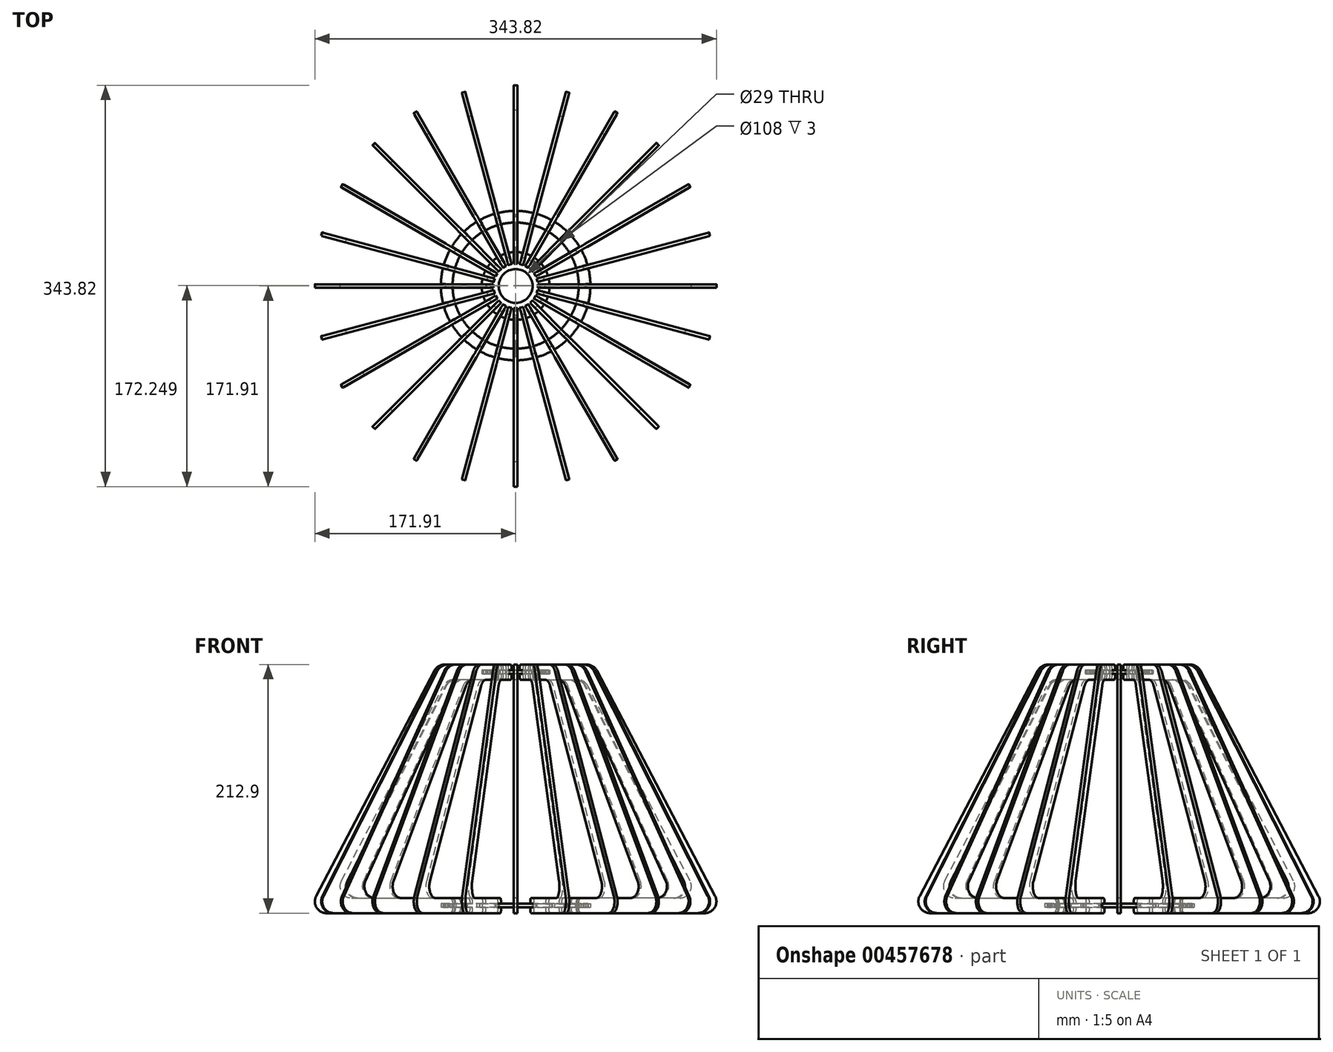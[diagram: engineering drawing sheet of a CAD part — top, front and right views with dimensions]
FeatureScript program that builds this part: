
annotation { "Feature Type Name" : "Feature", "Feature Type Description" : "" }
export const myFeature = defineFeature(function(context is Context, id is Id, definition is map)
    precondition{}
    {
        {
            var Q0;
            Q0=qCreatedBy(makeId("Top.planeOp"),FACE);
            var sketch = newSketch(context, id + "F0", { "sketchPlane" : qUnion([Q0])});
            skCircle(sketch, "E0", {"center": v(0, 0) * mm, "radius": 14.5 * mm});
            skArc(sketch, "E1", {"start": v(-1.45, 29) * mm, "mid": v(-3.79, 28.79) * mm, "end": v(-6.1, 28.39) * mm});
            skLineSegment(sketch, "E2", {"start": v(-1.45, 29) * mm, "end": v(-1.45, 25) * mm});
            skLineSegment(sketch, "E3", {"start": v(-1.45, 25) * mm, "end": v(1.45, 25) * mm});
            skLineSegment(sketch, "E4", {"start": v(1.45, 25) * mm, "end": v(1.45, 29) * mm});
            skLineSegment(sketch, "E5.1.0", {"start": v(-5.07, 24.52) * mm, "end": v(-6.1, 28.39) * mm});
            skLineSegment(sketch, "E5.1.1", {"start": v(-7.87, 23.77) * mm, "end": v(-5.07, 24.52) * mm});
            skLineSegment(sketch, "E5.1.2", {"start": v(-8.9, 27.64) * mm, "end": v(-7.87, 23.77) * mm});
            skLineSegment(sketch, "E5.2.0", {"start": v(-11.24, 22.38) * mm, "end": v(-13.24, 25.84) * mm});
            skLineSegment(sketch, "E5.2.1", {"start": v(-13.76, 20.93) * mm, "end": v(-11.24, 22.38) * mm});
            skLineSegment(sketch, "E5.2.2", {"start": v(-15.76, 24.39) * mm, "end": v(-13.76, 20.93) * mm});
            skLineSegment(sketch, "E5.3.0", {"start": v(-16.65, 18.7) * mm, "end": v(-19.48, 21.53) * mm});
            skLineSegment(sketch, "E5.3.1", {"start": v(-18.7, 16.65) * mm, "end": v(-16.65, 18.7) * mm});
            skLineSegment(sketch, "E5.3.2", {"start": v(-21.53, 19.48) * mm, "end": v(-18.7, 16.65) * mm});
            skLineSegment(sketch, "E5.4.0", {"start": v(-20.93, 13.76) * mm, "end": v(-24.39, 15.76) * mm});
            skLineSegment(sketch, "E5.4.1", {"start": v(-22.38, 11.24) * mm, "end": v(-20.93, 13.76) * mm});
            skLineSegment(sketch, "E5.4.2", {"start": v(-25.84, 13.24) * mm, "end": v(-22.38, 11.24) * mm});
            skLineSegment(sketch, "E5.5.0", {"start": v(-23.77, 7.87) * mm, "end": v(-27.64, 8.9) * mm});
            skLineSegment(sketch, "E5.5.1", {"start": v(-24.52, 5.07) * mm, "end": v(-23.77, 7.87) * mm});
            skLineSegment(sketch, "E5.5.2", {"start": v(-28.39, 6.1) * mm, "end": v(-24.52, 5.07) * mm});
            skLineSegment(sketch, "E5.6.0", {"start": v(-25, 1.45) * mm, "end": v(-29, 1.45) * mm});
            skLineSegment(sketch, "E5.6.1", {"start": v(-25, -1.45) * mm, "end": v(-25, 1.45) * mm});
            skLineSegment(sketch, "E5.6.2", {"start": v(-29, -1.45) * mm, "end": v(-25, -1.45) * mm});
            skLineSegment(sketch, "E5.7.0", {"start": v(-24.52, -5.07) * mm, "end": v(-28.39, -6.1) * mm});
            skLineSegment(sketch, "E5.7.1", {"start": v(-23.77, -7.87) * mm, "end": v(-24.52, -5.07) * mm});
            skLineSegment(sketch, "E5.7.2", {"start": v(-27.64, -8.9) * mm, "end": v(-23.77, -7.87) * mm});
            skLineSegment(sketch, "E5.8.0", {"start": v(-22.38, -11.24) * mm, "end": v(-25.84, -13.24) * mm});
            skLineSegment(sketch, "E5.8.1", {"start": v(-20.93, -13.76) * mm, "end": v(-22.38, -11.24) * mm});
            skLineSegment(sketch, "E5.8.2", {"start": v(-24.39, -15.76) * mm, "end": v(-20.93, -13.76) * mm});
            skLineSegment(sketch, "E5.9.0", {"start": v(-18.7, -16.65) * mm, "end": v(-21.53, -19.48) * mm});
            skLineSegment(sketch, "E5.9.1", {"start": v(-16.65, -18.7) * mm, "end": v(-18.7, -16.65) * mm});
            skLineSegment(sketch, "E5.9.2", {"start": v(-19.48, -21.53) * mm, "end": v(-16.65, -18.7) * mm});
            skLineSegment(sketch, "E5.10.0", {"start": v(-13.76, -20.93) * mm, "end": v(-15.76, -24.39) * mm});
            skLineSegment(sketch, "E5.10.1", {"start": v(-11.24, -22.38) * mm, "end": v(-13.76, -20.93) * mm});
            skLineSegment(sketch, "E5.10.2", {"start": v(-13.24, -25.84) * mm, "end": v(-11.24, -22.38) * mm});
            skArc(sketch, "E6.trimOffspring", {"start": v(-8.9, 27.64) * mm, "mid": v(-11.11, 26.83) * mm, "end": v(-13.24, 25.84) * mm});
            skArc(sketch, "E7.trimOffspring", {"start": v(-15.76, 24.39) * mm, "mid": v(-17.68, 23.04) * mm, "end": v(-19.48, 21.53) * mm});
            skArc(sketch, "E8.trimOffspring", {"start": v(-21.53, 19.48) * mm, "mid": v(-23.04, 17.68) * mm, "end": v(-24.39, 15.76) * mm});
            skArc(sketch, "E9.trimOffspring", {"start": v(-25.84, 13.24) * mm, "mid": v(-26.83, 11.11) * mm, "end": v(-27.64, 8.9) * mm});
            skArc(sketch, "E10.trimOffspring", {"start": v(-28.39, 6.1) * mm, "mid": v(-28.79, 3.79) * mm, "end": v(-29, 1.45) * mm});
            skArc(sketch, "E11.trimOffspring", {"start": v(-29, -1.45) * mm, "mid": v(-28.79, -3.79) * mm, "end": v(-28.39, -6.1) * mm});
            skArc(sketch, "E12.trimOffspring", {"start": v(-27.64, -8.9) * mm, "mid": v(-26.83, -11.11) * mm, "end": v(-25.84, -13.24) * mm});
            skArc(sketch, "E13.trimOffspring", {"start": v(-24.39, -15.76) * mm, "mid": v(-23.04, -17.68) * mm, "end": v(-21.53, -19.48) * mm});
            skArc(sketch, "E14.trimOffspring", {"start": v(-19.48, -21.53) * mm, "mid": v(-17.68, -23.04) * mm, "end": v(-15.76, -24.39) * mm});
            skArc(sketch, "E15.trimOffspring", {"start": v(6.1, 28.39) * mm, "mid": v(3.79, 28.79) * mm, "end": v(1.45, 29) * mm});
            skLineSegment(sketch, "E16.3.11.0", {"start": v(-5.07, -24.52) * mm, "end": v(-7.87, -23.77) * mm});
            skLineSegment(sketch, "E16.4.11.0", {"start": v(-7.87, -23.77) * mm, "end": v(-8.9, -27.64) * mm});
            skLineSegment(sketch, "E16.6.11.0", {"start": v(-6.1, -28.39) * mm, "end": v(-5.07, -24.52) * mm});
            skLineSegment(sketch, "E16.3.12.0", {"start": v(1.45, -25) * mm, "end": v(-1.45, -25) * mm});
            skLineSegment(sketch, "E16.4.12.0", {"start": v(-1.45, -25) * mm, "end": v(-1.45, -29) * mm});
            skLineSegment(sketch, "E16.6.12.0", {"start": v(1.45, -29) * mm, "end": v(1.45, -25) * mm});
            skLineSegment(sketch, "E16.3.13.0", {"start": v(7.87, -23.77) * mm, "end": v(5.07, -24.52) * mm});
            skLineSegment(sketch, "E16.4.13.0", {"start": v(5.07, -24.52) * mm, "end": v(6.1, -28.39) * mm});
            skLineSegment(sketch, "E16.6.13.0", {"start": v(8.9, -27.64) * mm, "end": v(7.87, -23.77) * mm});
            skLineSegment(sketch, "E17.3.14.0", {"start": v(13.76, -20.93) * mm, "end": v(11.24, -22.38) * mm});
            skLineSegment(sketch, "E17.4.14.0", {"start": v(11.24, -22.38) * mm, "end": v(13.24, -25.84) * mm});
            skLineSegment(sketch, "E17.6.14.0", {"start": v(15.76, -24.39) * mm, "end": v(13.76, -20.93) * mm});
            skLineSegment(sketch, "E17.3.15.0", {"start": v(18.7, -16.65) * mm, "end": v(16.65, -18.7) * mm});
            skLineSegment(sketch, "E17.4.15.0", {"start": v(16.65, -18.7) * mm, "end": v(19.48, -21.53) * mm});
            skLineSegment(sketch, "E17.6.15.0", {"start": v(21.53, -19.48) * mm, "end": v(18.7, -16.65) * mm});
            skArc(sketch, "E18.trimOffspring", {"start": v(15.76, -24.39) * mm, "mid": v(17.68, -23.04) * mm, "end": v(19.48, -21.53) * mm});
            skArc(sketch, "E19.trimOffspring", {"start": v(8.9, -27.64) * mm, "mid": v(11.11, -26.83) * mm, "end": v(13.24, -25.84) * mm});
            skArc(sketch, "E20.trimOffspring", {"start": v(1.45, -29) * mm, "mid": v(3.79, -28.79) * mm, "end": v(6.1, -28.39) * mm});
            skArc(sketch, "E21.trimOffspring", {"start": v(-6.1, -28.39) * mm, "mid": v(-3.79, -28.79) * mm, "end": v(-1.45, -29) * mm});
            skArc(sketch, "E22.trimOffspring", {"start": v(-13.24, -25.84) * mm, "mid": v(-11.11, -26.83) * mm, "end": v(-8.9, -27.64) * mm});
            skLineSegment(sketch, "E23.3.16.0", {"start": v(22.38, -11.24) * mm, "end": v(20.93, -13.76) * mm});
            skLineSegment(sketch, "E23.4.16.0", {"start": v(20.93, -13.76) * mm, "end": v(24.39, -15.76) * mm});
            skLineSegment(sketch, "E23.6.16.0", {"start": v(25.84, -13.24) * mm, "end": v(22.38, -11.24) * mm});
            skLineSegment(sketch, "E23.3.17.0", {"start": v(24.52, -5.07) * mm, "end": v(23.77, -7.87) * mm});
            skLineSegment(sketch, "E23.4.17.0", {"start": v(23.77, -7.87) * mm, "end": v(27.64, -8.9) * mm});
            skLineSegment(sketch, "E23.6.17.0", {"start": v(28.39, -6.1) * mm, "end": v(24.52, -5.07) * mm});
            skLineSegment(sketch, "E23.3.18.0", {"start": v(25, 1.45) * mm, "end": v(25, -1.45) * mm});
            skLineSegment(sketch, "E23.4.18.0", {"start": v(25, -1.45) * mm, "end": v(29, -1.45) * mm});
            skLineSegment(sketch, "E23.6.18.0", {"start": v(29, 1.45) * mm, "end": v(25, 1.45) * mm});
            skLineSegment(sketch, "E23.3.19.0", {"start": v(23.77, 7.87) * mm, "end": v(24.52, 5.07) * mm});
            skLineSegment(sketch, "E23.4.19.0", {"start": v(24.52, 5.07) * mm, "end": v(28.39, 6.1) * mm});
            skLineSegment(sketch, "E23.6.19.0", {"start": v(27.64, 8.9) * mm, "end": v(23.77, 7.87) * mm});
            skLineSegment(sketch, "E23.3.20.0", {"start": v(20.93, 13.76) * mm, "end": v(22.38, 11.24) * mm});
            skLineSegment(sketch, "E23.4.20.0", {"start": v(22.38, 11.24) * mm, "end": v(25.84, 13.24) * mm});
            skLineSegment(sketch, "E23.6.20.0", {"start": v(24.39, 15.76) * mm, "end": v(20.93, 13.76) * mm});
            skLineSegment(sketch, "E23.3.21.0", {"start": v(16.65, 18.7) * mm, "end": v(18.7, 16.65) * mm});
            skLineSegment(sketch, "E23.4.21.0", {"start": v(18.7, 16.65) * mm, "end": v(21.53, 19.48) * mm});
            skLineSegment(sketch, "E23.6.21.0", {"start": v(19.48, 21.53) * mm, "end": v(16.65, 18.7) * mm});
            skLineSegment(sketch, "E23.3.22.0", {"start": v(11.24, 22.38) * mm, "end": v(13.76, 20.93) * mm});
            skLineSegment(sketch, "E23.4.22.0", {"start": v(13.76, 20.93) * mm, "end": v(15.76, 24.39) * mm});
            skLineSegment(sketch, "E23.6.22.0", {"start": v(13.24, 25.84) * mm, "end": v(11.24, 22.38) * mm});
            skLineSegment(sketch, "E23.3.23.0", {"start": v(5.07, 24.52) * mm, "end": v(7.87, 23.77) * mm});
            skLineSegment(sketch, "E23.4.23.0", {"start": v(7.87, 23.77) * mm, "end": v(8.9, 27.64) * mm});
            skLineSegment(sketch, "E23.6.23.0", {"start": v(6.1, 28.39) * mm, "end": v(5.07, 24.52) * mm});
            skArc(sketch, "E24.trimOffspring", {"start": v(13.24, 25.84) * mm, "mid": v(11.11, 26.83) * mm, "end": v(8.9, 27.64) * mm});
            skArc(sketch, "E25.trimOffspring", {"start": v(19.48, 21.53) * mm, "mid": v(17.68, 23.04) * mm, "end": v(15.76, 24.39) * mm});
            skArc(sketch, "E26.trimOffspring", {"start": v(24.39, 15.76) * mm, "mid": v(23.04, 17.68) * mm, "end": v(21.53, 19.48) * mm});
            skArc(sketch, "E27.trimOffspring", {"start": v(27.64, 8.9) * mm, "mid": v(26.83, 11.11) * mm, "end": v(25.84, 13.24) * mm});
            skArc(sketch, "E28.trimOffspring", {"start": v(29, 1.45) * mm, "mid": v(28.79, 3.79) * mm, "end": v(28.39, 6.1) * mm});
            skArc(sketch, "E29.trimOffspring", {"start": v(28.39, -6.1) * mm, "mid": v(28.79, -3.79) * mm, "end": v(29, -1.45) * mm});
            skArc(sketch, "E30.trimOffspring", {"start": v(25.84, -13.24) * mm, "mid": v(26.83, -11.11) * mm, "end": v(27.64, -8.9) * mm});
            skArc(sketch, "E31.trimOffspring", {"start": v(21.53, -19.48) * mm, "mid": v(23.04, -17.68) * mm, "end": v(24.39, -15.76) * mm});
            skSolve(sketch);
        }
        {
            var Q0;
            Q0 = qSketchRegion(id + "F0", true);
            extrude(context, id + "F1", {"entities" : qUnion([Q0]), "depth" : 3 * mm});
        }
        {
            var Q0;
            Q0=qCreatedBy(makeId("Right.planeOp"),FACE);
            var sketch = newSketch(context, id + "F2", { "sketchPlane" : qUnion([Q0])});
            skLineSegment(sketch, "E32", {"start": v(19, 2.9) * mm, "end": v(25, 2.9) * mm});
            skLineSegment(sketch, "E33", {"start": v(25, 2.9) * mm, "end": v(25, 0) * mm});
            skLineSegment(sketch, "E34", {"start": v(19, 0) * mm, "end": v(25, 0) * mm});
            skLineSegment(sketch, "E35", {"start": v(19, 0) * mm, "end": v(19, -2) * mm});
            skLineSegment(sketch, "E36", {"start": v(22, -5) * mm, "end": v(52.95, -5) * mm});
            skLineSegment(sketch, "E37", {"start": v(60.87, 7.9) * mm, "end": v(22, 7.9) * mm});
            skLineSegment(sketch, "E38", {"start": v(19, 4.9) * mm, "end": v(19, 2.9) * mm});
            skPoint(sketch, "E39.visualSharp", {"position": v(19, 7.9) * mm});
            skArc(sketch, "E39.filletArc", {"start": v(22, 7.9) * mm, "mid": v(19.88, 7.02) * mm, "end": v(19, 4.9) * mm});
            skPoint(sketch, "E40.visualSharp", {"position": v(19, -5) * mm});
            skArc(sketch, "E40.filletArc", {"start": v(19, -2) * mm, "mid": v(19.88, -4.12) * mm, "end": v(22, -5) * mm});
            skLineSegment(sketch, "E41", {"start": v(54, -197.1) * mm, "end": v(60, -197.1) * mm});
            skLineSegment(sketch, "E42", {"start": v(60, -197.1) * mm, "end": v(60, -200) * mm});
            skLineSegment(sketch, "E43", {"start": v(54, -200) * mm, "end": v(60, -200) * mm});
            skLineSegment(sketch, "E44", {"start": v(54, -200) * mm, "end": v(54, -202) * mm});
            skLineSegment(sketch, "E45", {"start": v(57, -205) * mm, "end": v(161.9, -205) * mm});
            skLineSegment(sketch, "E46", {"start": v(140.47, -192.1) * mm, "end": v(57, -192.1) * mm});
            skLineSegment(sketch, "E47", {"start": v(54, -195.1) * mm, "end": v(54, -197.1) * mm});
            skPoint(sketch, "E48.visualSharp", {"position": v(54, -192.1) * mm});
            skArc(sketch, "E48.filletArc", {"start": v(57, -192.1) * mm, "mid": v(54.88, -192.98) * mm, "end": v(54, -195.1) * mm});
            skPoint(sketch, "E49.visualSharp", {"position": v(54, -205) * mm});
            skArc(sketch, "E49.filletArc", {"start": v(54, -202) * mm, "mid": v(54.88, -204.12) * mm, "end": v(57, -205) * mm});
            skLineSegment(sketch, "E50", {"start": v(149.33, -177.46) * mm, "end": v(61.8, -10.36) * mm});
            skLineSegment(sketch, "E51.0", {"start": v(170.76, -190.36) * mm, "end": v(69.73, 2.54) * mm});
            skPoint(sketch, "E52.visualSharp", {"position": v(178.43, -205) * mm});
            skArc(sketch, "E52.filletArc", {"start": v(161.9, -205) * mm, "mid": v(170.46, -200.18) * mm, "end": v(170.76, -190.36) * mm});
            skPoint(sketch, "E53.visualSharp", {"position": v(157, -192.1) * mm});
            skArc(sketch, "E53.filletArc", {"start": v(140.47, -192.1) * mm, "mid": v(149.03, -187.28) * mm, "end": v(149.33, -177.46) * mm});
            skPoint(sketch, "E54.visualSharp", {"position": v(59, -5) * mm});
            skArc(sketch, "E54.filletArc", {"start": v(61.8, -10.36) * mm, "mid": v(58.13, -6.44) * mm, "end": v(52.95, -5) * mm});
            skPoint(sketch, "E55.visualSharp", {"position": v(66.92, 7.9) * mm});
            skArc(sketch, "E55.filletArc", {"start": v(69.73, 2.54) * mm, "mid": v(66.04, 6.46) * mm, "end": v(60.87, 7.9) * mm});
            skSolve(sketch);
        }
        {
            var Q0;
            Q0 = qSketchRegion(id + "F2", true);
            extrude(context, id + "F3", {"entities" : qUnion([Q0]), "endBound" : BoundingType.SYMMETRIC, "depth" : 3 * mm});
        }
        {
            var Q0;
            Q0=qCreatedBy(makeId("Top.planeOp"),FACE);
            cPlane(context, id + "F4", {"entities" : qUnion([Q0]), "cplaneType" : CPlaneType.OFFSET, "offset" : 200 * mm, "oppositeDirection" : true, "width" : 150 * mm, "height" : 150 * mm});
        }
        {
            var Q0;
            Q0=qCreatedBy(id+"F4.planeOp",FACE);
            var sketch = newSketch(context, id + "F5", { "sketchPlane" : qUnion([Q0])});
            skCircle(sketch, "E56", {"center": v(0, 0.34) * mm, "radius": 54 * mm});
            skArc(sketch, "E57", {"start": v(-1.45, 64.34) * mm, "mid": v(-8.36, 63.8) * mm, "end": v(-15.16, 62.53) * mm});
            skLineSegment(sketch, "E58", {"start": v(-1.45, 64.34) * mm, "end": v(-1.45, 60.34) * mm});
            skLineSegment(sketch, "E59", {"start": v(-1.45, 60.34) * mm, "end": v(1.45, 60.34) * mm});
            skLineSegment(sketch, "E60", {"start": v(1.45, 60.34) * mm, "end": v(1.45, 64.34) * mm});
            skLineSegment(sketch, "E61.1.0", {"start": v(-14.13, 58.67) * mm, "end": v(-15.16, 62.53) * mm});
            skLineSegment(sketch, "E61.1.1", {"start": v(-16.93, 57.92) * mm, "end": v(-14.13, 58.67) * mm});
            skLineSegment(sketch, "E61.1.2", {"start": v(-17.97, 61.78) * mm, "end": v(-16.93, 57.92) * mm});
            skLineSegment(sketch, "E61.2.0", {"start": v(-28.74, 53.03) * mm, "end": v(-30.74, 56.49) * mm});
            skLineSegment(sketch, "E61.2.1", {"start": v(-31.26, 51.58) * mm, "end": v(-28.74, 53.03) * mm});
            skLineSegment(sketch, "E61.2.2", {"start": v(-33.26, 55.04) * mm, "end": v(-31.26, 51.58) * mm});
            skLineSegment(sketch, "E61.3.0", {"start": v(-41.4, 43.8) * mm, "end": v(-44.23, 46.62) * mm});
            skLineSegment(sketch, "E61.3.1", {"start": v(-43.45, 41.74) * mm, "end": v(-41.4, 43.8) * mm});
            skLineSegment(sketch, "E61.3.2", {"start": v(-46.28, 44.57) * mm, "end": v(-43.45, 41.74) * mm});
            skLineSegment(sketch, "E61.4.0", {"start": v(-51.24, 31.6) * mm, "end": v(-54.7, 33.6) * mm});
            skLineSegment(sketch, "E61.4.1", {"start": v(-52.69, 29.08) * mm, "end": v(-51.24, 31.6) * mm});
            skLineSegment(sketch, "E61.4.2", {"start": v(-56.15, 31.08) * mm, "end": v(-52.69, 29.08) * mm});
            skLineSegment(sketch, "E61.5.0", {"start": v(-57.58, 17.27) * mm, "end": v(-61.44, 18.3) * mm});
            skLineSegment(sketch, "E61.5.1", {"start": v(-58.33, 14.47) * mm, "end": v(-57.58, 17.27) * mm});
            skLineSegment(sketch, "E61.5.2", {"start": v(-62.2, 15.5) * mm, "end": v(-58.33, 14.47) * mm});
            skLineSegment(sketch, "E61.6.0", {"start": v(-60, 1.79) * mm, "end": v(-64, 1.79) * mm});
            skLineSegment(sketch, "E61.6.1", {"start": v(-60, -1.11) * mm, "end": v(-60, 1.79) * mm});
            skLineSegment(sketch, "E61.6.2", {"start": v(-64, -1.11) * mm, "end": v(-60, -1.11) * mm});
            skLineSegment(sketch, "E61.7.0", {"start": v(-58.33, -13.79) * mm, "end": v(-62.2, -14.82) * mm});
            skLineSegment(sketch, "E61.7.1", {"start": v(-57.58, -16.6) * mm, "end": v(-58.33, -13.79) * mm});
            skLineSegment(sketch, "E61.7.2", {"start": v(-61.44, -17.63) * mm, "end": v(-57.58, -16.6) * mm});
            skLineSegment(sketch, "E61.8.0", {"start": v(-52.69, -28.4) * mm, "end": v(-56.15, -30.4) * mm});
            skLineSegment(sketch, "E61.8.1", {"start": v(-51.24, -30.92) * mm, "end": v(-52.69, -28.4) * mm});
            skLineSegment(sketch, "E61.8.2", {"start": v(-54.7, -32.92) * mm, "end": v(-51.24, -30.92) * mm});
            skLineSegment(sketch, "E61.9.0", {"start": v(-43.45, -41.06) * mm, "end": v(-46.28, -43.9) * mm});
            skLineSegment(sketch, "E61.9.1", {"start": v(-41.4, -43.11) * mm, "end": v(-43.45, -41.06) * mm});
            skLineSegment(sketch, "E61.9.2", {"start": v(-44.23, -45.94) * mm, "end": v(-41.4, -43.11) * mm});
            skLineSegment(sketch, "E61.10.0", {"start": v(-31.26, -50.9) * mm, "end": v(-33.26, -54.36) * mm});
            skLineSegment(sketch, "E61.10.1", {"start": v(-28.74, -52.35) * mm, "end": v(-31.26, -50.9) * mm});
            skLineSegment(sketch, "E61.10.2", {"start": v(-30.74, -55.81) * mm, "end": v(-28.74, -52.35) * mm});
            skArc(sketch, "E62.trimOffspring", {"start": v(-17.97, 61.78) * mm, "mid": v(-24.5, 59.48) * mm, "end": v(-30.74, 56.49) * mm});
            skArc(sketch, "E63.trimOffspring", {"start": v(-33.26, 55.04) * mm, "mid": v(-38.97, 51.13) * mm, "end": v(-44.23, 46.62) * mm});
            skArc(sketch, "E64.trimOffspring", {"start": v(-46.28, 44.57) * mm, "mid": v(-50.79, 39.31) * mm, "end": v(-54.7, 33.6) * mm});
            skArc(sketch, "E65.trimOffspring", {"start": v(-56.15, 31.08) * mm, "mid": v(-59.14, 24.84) * mm, "end": v(-61.44, 18.3) * mm});
            skArc(sketch, "E66.trimOffspring", {"start": v(-62.2, 15.5) * mm, "mid": v(-63.47, 8.7) * mm, "end": v(-64, 1.79) * mm});
            skArc(sketch, "E67.trimOffspring", {"start": v(-64, -1.11) * mm, "mid": v(-63.47, -8.02) * mm, "end": v(-62.2, -14.82) * mm});
            skArc(sketch, "E68.trimOffspring", {"start": v(-61.44, -17.63) * mm, "mid": v(-59.14, -24.16) * mm, "end": v(-56.15, -30.4) * mm});
            skArc(sketch, "E69.trimOffspring", {"start": v(-54.7, -32.92) * mm, "mid": v(-50.79, -38.63) * mm, "end": v(-46.28, -43.9) * mm});
            skArc(sketch, "E70.trimOffspring", {"start": v(-44.23, -45.94) * mm, "mid": v(-38.97, -50.45) * mm, "end": v(-33.26, -54.36) * mm});
            skArc(sketch, "E71.trimOffspring", {"start": v(15.16, 62.53) * mm, "mid": v(8.36, 63.8) * mm, "end": v(1.45, 64.34) * mm});
            skLineSegment(sketch, "E72.3.11.0", {"start": v(-14.13, -58) * mm, "end": v(-16.93, -57.24) * mm});
            skLineSegment(sketch, "E72.4.11.0", {"start": v(-16.93, -57.24) * mm, "end": v(-17.97, -61.1) * mm});
            skLineSegment(sketch, "E72.6.11.0", {"start": v(-15.16, -61.86) * mm, "end": v(-14.13, -58) * mm});
            skLineSegment(sketch, "E72.3.12.0", {"start": v(1.45, -59.66) * mm, "end": v(-1.45, -59.66) * mm});
            skLineSegment(sketch, "E72.4.12.0", {"start": v(-1.45, -59.66) * mm, "end": v(-1.45, -63.66) * mm});
            skLineSegment(sketch, "E72.6.12.0", {"start": v(1.45, -63.66) * mm, "end": v(1.45, -59.66) * mm});
            skLineSegment(sketch, "E72.3.13.0", {"start": v(16.93, -57.24) * mm, "end": v(14.13, -58) * mm});
            skLineSegment(sketch, "E72.4.13.0", {"start": v(14.13, -58) * mm, "end": v(15.16, -61.86) * mm});
            skLineSegment(sketch, "E72.6.13.0", {"start": v(17.97, -61.1) * mm, "end": v(16.93, -57.24) * mm});
            skLineSegment(sketch, "E73.3.14.0", {"start": v(31.26, -50.9) * mm, "end": v(28.74, -52.35) * mm});
            skLineSegment(sketch, "E73.4.14.0", {"start": v(28.74, -52.35) * mm, "end": v(30.74, -55.81) * mm});
            skLineSegment(sketch, "E73.6.14.0", {"start": v(33.26, -54.36) * mm, "end": v(31.26, -50.9) * mm});
            skLineSegment(sketch, "E73.3.15.0", {"start": v(43.45, -41.06) * mm, "end": v(41.4, -43.11) * mm});
            skLineSegment(sketch, "E73.4.15.0", {"start": v(41.4, -43.11) * mm, "end": v(44.23, -45.94) * mm});
            skLineSegment(sketch, "E73.6.15.0", {"start": v(46.28, -43.9) * mm, "end": v(43.45, -41.06) * mm});
            skArc(sketch, "E74.trimOffspring", {"start": v(33.26, -54.36) * mm, "mid": v(38.97, -50.45) * mm, "end": v(44.23, -45.94) * mm});
            skArc(sketch, "E75.trimOffspring", {"start": v(17.97, -61.1) * mm, "mid": v(24.5, -58.8) * mm, "end": v(30.74, -55.81) * mm});
            skArc(sketch, "E76.trimOffspring", {"start": v(1.45, -63.66) * mm, "mid": v(8.36, -63.13) * mm, "end": v(15.16, -61.86) * mm});
            skArc(sketch, "E77.trimOffspring", {"start": v(-15.16, -61.86) * mm, "mid": v(-8.36, -63.13) * mm, "end": v(-1.45, -63.66) * mm});
            skArc(sketch, "E78.trimOffspring", {"start": v(-30.74, -55.81) * mm, "mid": v(-24.5, -58.8) * mm, "end": v(-17.97, -61.1) * mm});
            skLineSegment(sketch, "E79.3.16.0", {"start": v(52.69, -28.4) * mm, "end": v(51.24, -30.92) * mm});
            skLineSegment(sketch, "E79.4.16.0", {"start": v(51.24, -30.92) * mm, "end": v(54.7, -32.92) * mm});
            skLineSegment(sketch, "E79.6.16.0", {"start": v(56.15, -30.4) * mm, "end": v(52.69, -28.4) * mm});
            skLineSegment(sketch, "E79.3.17.0", {"start": v(58.33, -13.79) * mm, "end": v(57.58, -16.6) * mm});
            skLineSegment(sketch, "E79.4.17.0", {"start": v(57.58, -16.6) * mm, "end": v(61.44, -17.63) * mm});
            skLineSegment(sketch, "E79.6.17.0", {"start": v(62.2, -14.82) * mm, "end": v(58.33, -13.79) * mm});
            skLineSegment(sketch, "E79.3.18.0", {"start": v(60, 1.79) * mm, "end": v(60, -1.11) * mm});
            skLineSegment(sketch, "E79.4.18.0", {"start": v(60, -1.11) * mm, "end": v(64, -1.11) * mm});
            skLineSegment(sketch, "E79.6.18.0", {"start": v(64, 1.79) * mm, "end": v(60, 1.79) * mm});
            skLineSegment(sketch, "E79.3.19.0", {"start": v(57.58, 17.27) * mm, "end": v(58.33, 14.47) * mm});
            skLineSegment(sketch, "E79.4.19.0", {"start": v(58.33, 14.47) * mm, "end": v(62.2, 15.5) * mm});
            skLineSegment(sketch, "E79.6.19.0", {"start": v(61.44, 18.3) * mm, "end": v(57.58, 17.27) * mm});
            skLineSegment(sketch, "E79.3.20.0", {"start": v(51.24, 31.6) * mm, "end": v(52.69, 29.08) * mm});
            skLineSegment(sketch, "E79.4.20.0", {"start": v(52.69, 29.08) * mm, "end": v(56.15, 31.08) * mm});
            skLineSegment(sketch, "E79.6.20.0", {"start": v(54.7, 33.6) * mm, "end": v(51.24, 31.6) * mm});
            skLineSegment(sketch, "E79.3.21.0", {"start": v(41.4, 43.8) * mm, "end": v(43.45, 41.74) * mm});
            skLineSegment(sketch, "E79.4.21.0", {"start": v(43.45, 41.74) * mm, "end": v(46.28, 44.57) * mm});
            skLineSegment(sketch, "E79.6.21.0", {"start": v(44.23, 46.62) * mm, "end": v(41.4, 43.8) * mm});
            skLineSegment(sketch, "E79.3.22.0", {"start": v(28.74, 53.03) * mm, "end": v(31.26, 51.58) * mm});
            skLineSegment(sketch, "E79.4.22.0", {"start": v(31.26, 51.58) * mm, "end": v(33.26, 55.04) * mm});
            skLineSegment(sketch, "E79.6.22.0", {"start": v(30.74, 56.49) * mm, "end": v(28.74, 53.03) * mm});
            skLineSegment(sketch, "E79.3.23.0", {"start": v(14.13, 58.67) * mm, "end": v(16.93, 57.92) * mm});
            skLineSegment(sketch, "E79.4.23.0", {"start": v(16.93, 57.92) * mm, "end": v(17.97, 61.78) * mm});
            skLineSegment(sketch, "E79.6.23.0", {"start": v(15.16, 62.53) * mm, "end": v(14.13, 58.67) * mm});
            skArc(sketch, "E80.trimOffspring", {"start": v(46.28, -43.9) * mm, "mid": v(50.79, -38.63) * mm, "end": v(54.7, -32.92) * mm});
            skArc(sketch, "E81.trimOffspring", {"start": v(56.15, -30.4) * mm, "mid": v(59.14, -24.16) * mm, "end": v(61.44, -17.63) * mm});
            skArc(sketch, "E82.trimOffspring", {"start": v(62.2, -14.82) * mm, "mid": v(63.47, -8.02) * mm, "end": v(64, -1.11) * mm});
            skArc(sketch, "E83.trimOffspring", {"start": v(64, 1.79) * mm, "mid": v(63.47, 8.7) * mm, "end": v(62.2, 15.5) * mm});
            skArc(sketch, "E84.trimOffspring", {"start": v(61.44, 18.3) * mm, "mid": v(59.14, 24.84) * mm, "end": v(56.15, 31.08) * mm});
            skArc(sketch, "E85.trimOffspring", {"start": v(54.7, 33.6) * mm, "mid": v(50.79, 39.31) * mm, "end": v(46.28, 44.57) * mm});
            skArc(sketch, "E86.trimOffspring", {"start": v(44.23, 46.62) * mm, "mid": v(38.97, 51.13) * mm, "end": v(33.26, 55.04) * mm});
            skArc(sketch, "E87.trimOffspring", {"start": v(30.74, 56.49) * mm, "mid": v(24.5, 59.48) * mm, "end": v(17.97, 61.78) * mm});
            skSolve(sketch);
        }
        {
            var Q0;
            Q0 = qSketchRegion(id + "F5", true);
            extrude(context, id + "F6", {"entities" : qUnion([Q0]), "depth" : 3 * mm});
        }
        {
            var Q0;
            Q0=makeQuery(id+"F3.opExtrude","SWEPT_BODY",BODY,{"disambiguationData":[OSD([sQuery(id+"F2.wireOp",EDGE,"E32"),sQuery(id+"F2.wireOp",EDGE,"E33"),sQuery(id+"F2.wireOp",EDGE,"E34"),sQuery(id+"F2.wireOp",EDGE,"E35"),sQuery(id+"F2.wireOp",EDGE,"E36"),sQuery(id+"F2.wireOp",EDGE,"E37"),sQuery(id+"F2.wireOp",EDGE,"E38"),sQuery(id+"F2.wireOp",EDGE,"E39.filletArc"),sQuery(id+"F2.wireOp",EDGE,"E40.filletArc"),sQuery(id+"F2.wireOp",EDGE,"E41"),sQuery(id+"F2.wireOp",EDGE,"E42"),sQuery(id+"F2.wireOp",EDGE,"E43"),sQuery(id+"F2.wireOp",EDGE,"E44"),sQuery(id+"F2.wireOp",EDGE,"E45"),sQuery(id+"F2.wireOp",EDGE,"E46"),sQuery(id+"F2.wireOp",EDGE,"E47"),sQuery(id+"F2.wireOp",EDGE,"E48.filletArc"),sQuery(id+"F2.wireOp",EDGE,"E49.filletArc"),sQuery(id+"F2.wireOp",EDGE,"E50"),sQuery(id+"F2.wireOp",EDGE,"E51.0"),sQuery(id+"F2.wireOp",EDGE,"E52.filletArc"),sQuery(id+"F2.wireOp",EDGE,"E53.filletArc"),sQuery(id+"F2.wireOp",EDGE,"E54.filletArc"),sQuery(id+"F2.wireOp",EDGE,"E55.filletArc")])]});
            var Q1;
            Q1=makeQuery(id+"F1.opExtrude","CAP_EDGE",EDGE,{"disambiguationData":[OSD([sQuery(id+"F0.wireOp",EDGE,"E0")])],"isStart":false});
            circularPattern(context, id + "F7", {"entities" : qUnion([Q0]), "axis" : qUnion([Q1]), "angle" : 360 * degree, "instanceCount" : 24, "equalSpace" : true});
        }
    });
